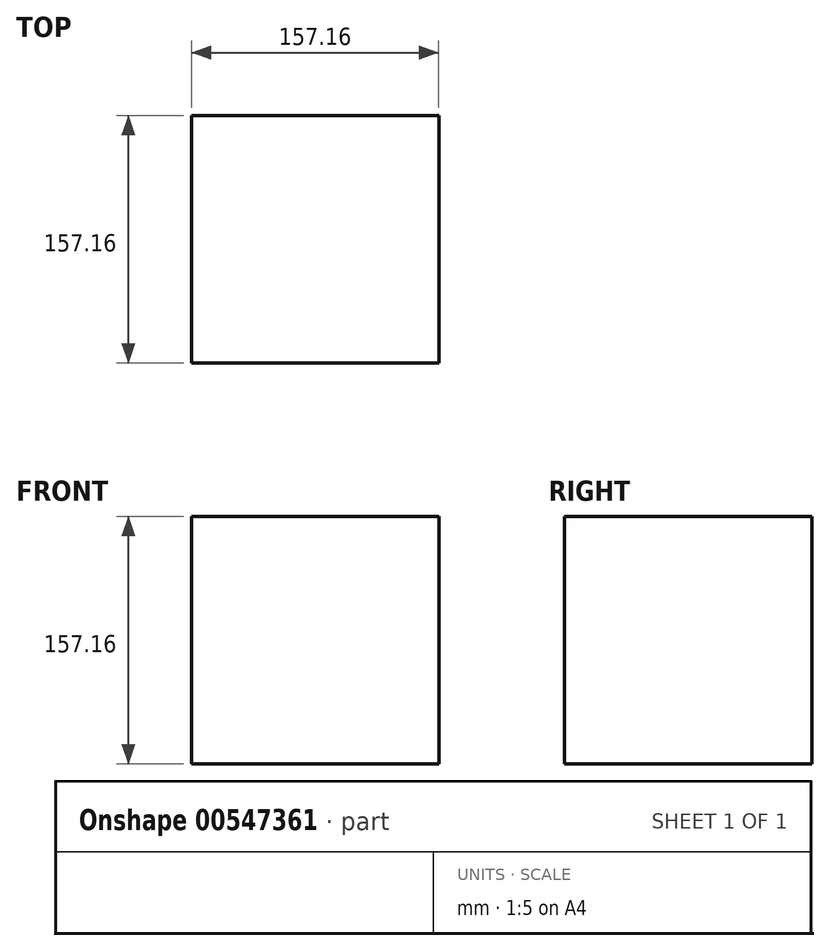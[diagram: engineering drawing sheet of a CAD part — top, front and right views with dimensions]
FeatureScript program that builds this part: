
annotation { "Feature Type Name" : "Feature", "Feature Type Description" : "" }
export const myFeature = defineFeature(function(context is Context, id is Id, definition is map)
    precondition{}
    {
        {
            var Q0;
            Q0=qCreatedBy(makeId("Top.planeOp"),FACE);
            var sketch = newSketch(context, id + "F0", { "sketchPlane" : qUnion([Q0])});
            skLineSegment(sketch, "E0.bottom", {"start": v(78.58, 78.58) * mm, "end": v(-78.58, 78.58) * mm});
            skLineSegment(sketch, "E0.top", {"start": v(78.58, -78.58) * mm, "end": v(-78.58, -78.58) * mm});
            skLineSegment(sketch, "E0.left", {"start": v(78.58, 78.58) * mm, "end": v(78.58, -78.58) * mm});
            skLineSegment(sketch, "E0.right", {"start": v(-78.58, 78.58) * mm, "end": v(-78.58, -78.58) * mm});
            skPoint(sketch, "E0.middle", {"position": v(0, 0) * mm});
            skSolve(sketch);
        }
        {
            var Q0;
            Q0 = qSketchRegion(id + "F0", true);
            extrude(context, id + "F1", {"entities" : qUnion([Q0]), "depth" : 157.16 * mm, "offsetDistance" : 25.4 * mm});
        }
    });
